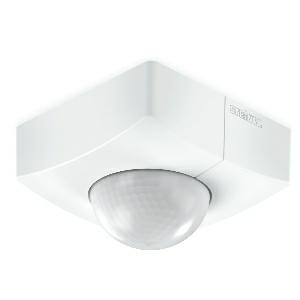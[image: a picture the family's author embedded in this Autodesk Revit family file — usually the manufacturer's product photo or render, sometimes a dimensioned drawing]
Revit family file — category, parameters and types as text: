
# Revit family: is_345_mx_highbay_010492
name_source: partatom
category: Elektroinstallationen
revit_build: Autodesk Revit 2016 (Build: 20190508_0715(x64)
units: mm (PartAtom-declared; Revit-internal decimal feet)

## family parameters
Basisbauteil = Fläche
Beim Laden mit Abzugskörper schneiden = Nein
Bemaßung runder Anschluss = Durchmesser verwenden
Beschriftungsausrichtung beibehalten = Nein
Gemeinsam genutzt = Nein
Raumberechnungspunkt = Nein
Teiletyp = Normal

## types (1)
- IS 345 MX Highbay
    Apparent Load = 0 VA
    Beschreibung = Type: Motion detectors; Dimensions (L x W x H): 65 x 95 x 95 mm; Mains power supply: 220 – 240 V / 50 – 60 Hz; Sensor Technology: passive infrared; Application, place: Indoors; Application, room: high-bay warehouse, Indoors; Installation site: ceiling; Installation: Surface wiring; Switching zones: 280 switching zones; Electronic scalability: No; Mechanical scalability: No; Mounting height: 4,00 – 14,00 m; Optimum mounting height: 12 m; Detection angle: 360 °; Angle of aperture: 9 °; Sneak-by guard: Yes; Capability of masking out individual segments: Yes; Reach, radial: 30 x 4 m (120 m²); Reach, tangential: 30 x 4 m (120 m²); Twilight setting TEACH: Yes; Twilight setting: 2 – 1000 lx; Time setting: 5 sec – 15 min; Switching output 1, resistive: 2000 W; Switching output 1, number of LEDs / fluorescent lamps: 8 pcs.; Constant-lighting control: No; Basic light level function: No; Functions: Normal / test mode, Manual ON / ON-OFF; Settings via: Remote control, Potentiometers, Smart Remote; With remote control: No; Interconnection: Yes; IP-rating: IP54; Material: Plastic; Ambient temperature: -20 – 50 °C; Colour: white; Colour, RAL: 9003; Manufacturer's Warranty: 5 years; Version: COM1 - surface, sq.; PU1, EAN: 4007841010492
    Height = 95 mm
    Hersteller = Steinel
    Length = 65 mm
    Maximum range = 3.441 m
    ModVariant = Nein
    Modell = 010492
    Mounting Place = Ceiling
    Mounting Type = Surface mounted
    Number of Poles = 1
    OnlyDefault = Ja
    Power Factor = 1
    Product Name = IS 345 MX Highbay
    Product group = Sensor-switched outdoor light
    ProductGroupID = 3
    Protection Class = Protection class
    Protection Degree = IP 54
    RlxData = <blob elided: 194949 chars, md5=946bd271>
    Sensor characteristics = Circular 300°-360°
    Sensor type = Passive (infrared)
    SensorDataFile = <blob elided: 170895 chars, md5=da062800>
    Type of entry = Motion
    Typenbild = produkt1_010492.jpg
    Typenkommentare = Product without accessories
    URL = http://relux.com
    VarID = ---
    Voltage = 0 V
    Vorgabe-Ansicht = 1800 mm
    Weight = 0.00 kg
    Width = 95 mm

## geometry (parser evidence)
native form markers: Sweep x16
no freeform markers — native parametric forms only
